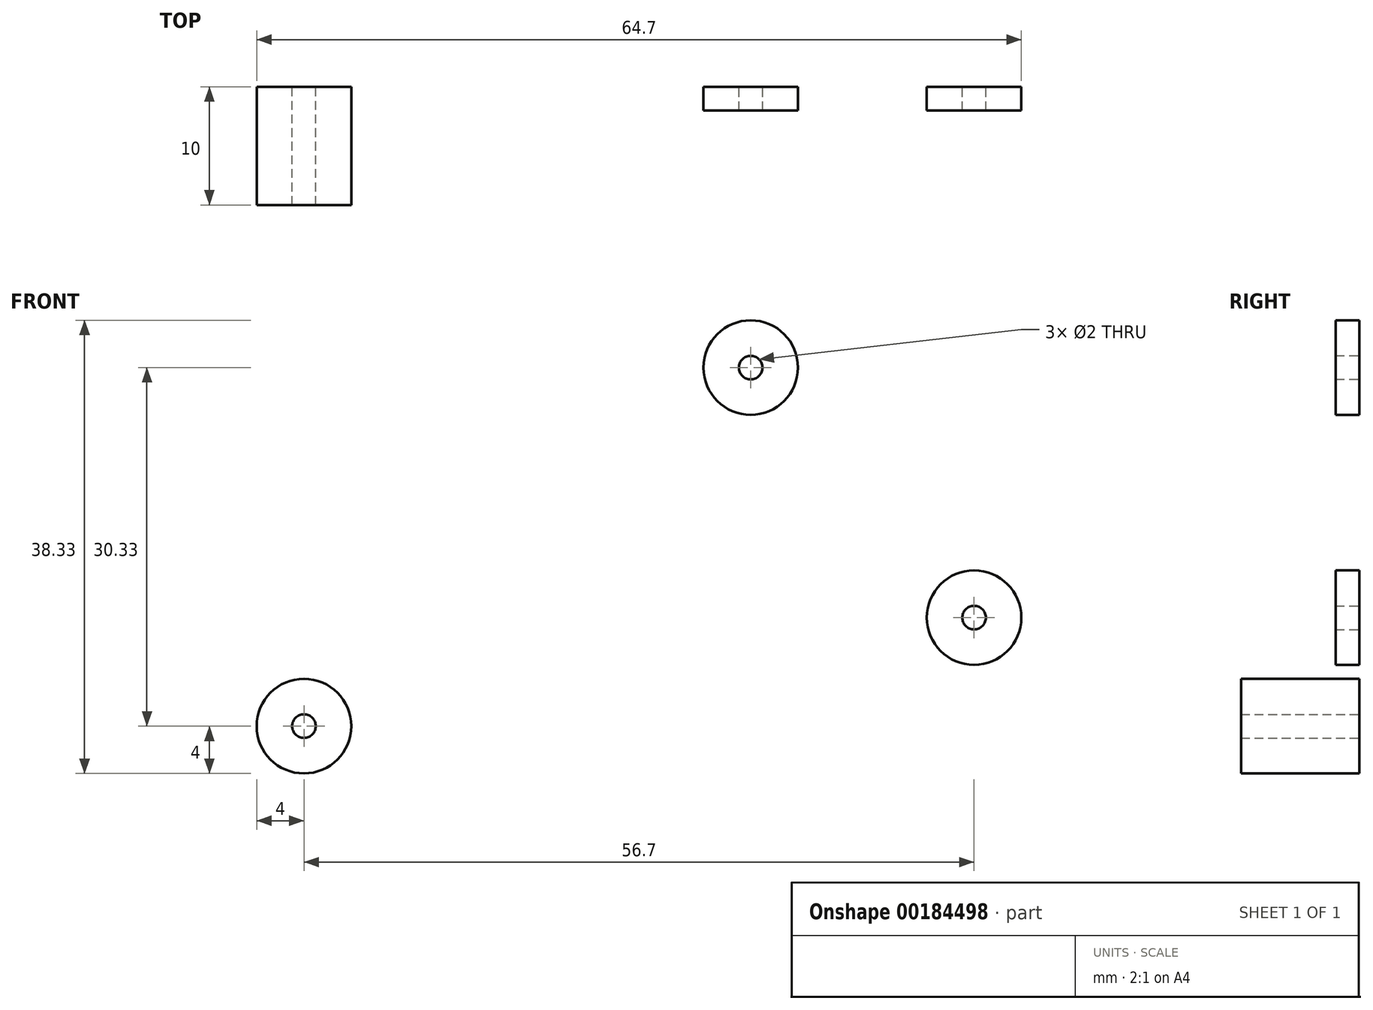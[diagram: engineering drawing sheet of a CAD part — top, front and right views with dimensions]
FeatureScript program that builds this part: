
annotation { "Feature Type Name" : "Feature", "Feature Type Description" : "" }
export const myFeature = defineFeature(function(context is Context, id is Id, definition is map)
    precondition{}
    {
        {
            var Q0;
            Q0=qCreatedBy(makeId("Front.planeOp"),FACE);
            var sketch = newSketch(context, id + "F0", { "sketchPlane" : qUnion([Q0])});
            skCircle(sketch, "E0", {"center": v(0, 0) * mm, "radius": 4 * mm});
            skCircle(sketch, "E1", {"center": v(0, 0) * mm, "radius": 1 * mm});
            skSolve(sketch);
        }
        {
            var Q0;
            Q0 = qSketchRegion(id + "F0", true);
            extrude(context, id + "F1", {"entities" : qUnion([Q0]), "depth" : 2 * mm});
        }
        {
            var Q0;
            Q0=qCreatedBy(makeId("Front.planeOp"),FACE);
            var sketch = newSketch(context, id + "F2", { "sketchPlane" : qUnion([Q0])});
            skCircle(sketch, "E2", {"center": v(-37.8, -30.33) * mm, "radius": 4 * mm});
            skCircle(sketch, "E3", {"center": v(-37.8, -30.33) * mm, "radius": 1 * mm});
            skSolve(sketch);
        }
        {
            var Q0;
            Q0 = qSketchRegion(id + "F2", true);
            extrude(context, id + "F3", {"entities" : qUnion([Q0]), "depth" : 10 * mm});
        }
        {
            var Q0;
            Q0=qCreatedBy(makeId("Front.planeOp"),FACE);
            var sketch = newSketch(context, id + "F4", { "sketchPlane" : qUnion([Q0])});
            skCircle(sketch, "E4", {"center": v(18.9, -21.15) * mm, "radius": 4 * mm});
            skCircle(sketch, "E5", {"center": v(18.9, -21.15) * mm, "radius": 1 * mm});
            skSolve(sketch);
        }
        {
            var Q0;
            Q0=makeQuery(id+"F4.imprint","IMPRINT",FACE,{"disambiguationData":[TD([[makeQuery(id+"F4.imprint","IMPRINT",EDGE,{"derivedFrom":sQuery(id+"F4.wireOp",EDGE,"E4")}),1.0]])]});
            extrude(context, id + "F5", {"entities" : qUnion([Q0]), "depth" : 2 * mm});
        }
    });
